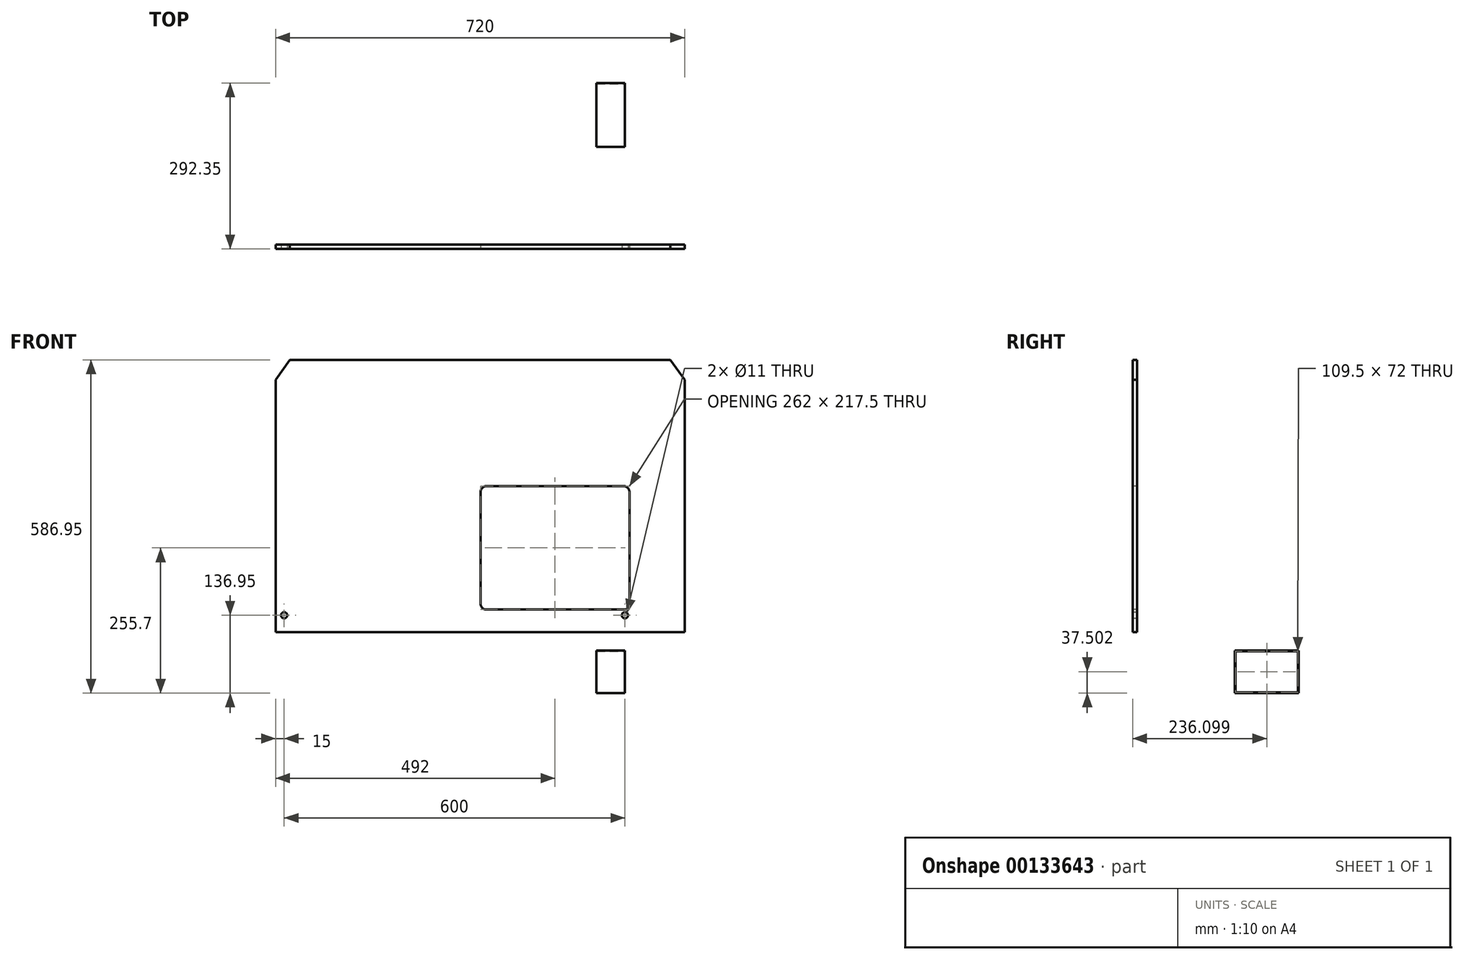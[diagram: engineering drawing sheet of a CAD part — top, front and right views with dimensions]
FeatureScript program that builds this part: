
annotation { "Feature Type Name" : "Feature", "Feature Type Description" : "" }
export const myFeature = defineFeature(function(context is Context, id is Id, definition is map)
    precondition{}
    {
        {
            var Q0;
            Q0=qCreatedBy(makeId("Front.planeOp"),FACE);
            var sketch = newSketch(context, id + "F0", { "sketchPlane" : qUnion([Q0])});
            skLineSegment(sketch, "E0.bottom", {"start": v(-196, 100) * mm, "end": v(-50, 100) * mm});
            skLineSegment(sketch, "E0.top", {"start": v(-196, 207.5) * mm, "end": v(-50, 207.5) * mm});
            skLineSegment(sketch, "E0.left", {"start": v(-196, 100) * mm, "end": v(-196, 207.5) * mm});
            skLineSegment(sketch, "E0.right", {"start": v(-50, 100) * mm, "end": v(-50, 207.5) * mm});
            skLineSegment(sketch, "E1.top", {"start": v(-196, 30) * mm, "end": v(-50, 30) * mm});
            skLineSegment(sketch, "E1.left", {"start": v(-196, 100) * mm, "end": v(-196, 30) * mm});
            skLineSegment(sketch, "E1.right", {"start": v(-50, 100) * mm, "end": v(-50, 30) * mm});
            skLineSegment(sketch, "E2", {"start": v(-196, 207.5) * mm, "end": v(-236, 202.5) * mm});
            skLineSegment(sketch, "E3", {"start": v(-236, 202.5) * mm, "end": v(-236, 105) * mm});
            skLineSegment(sketch, "E4", {"start": v(-236, 105) * mm, "end": v(-196, 100) * mm});
            skLineSegment(sketch, "E5", {"start": v(-123, 207.5) * mm, "end": v(-123, 30) * mm, "construction": true});
            skLineSegment(sketch, "E6", {"start": v(-50, 207.5) * mm, "end": v(-10, 202.5) * mm});
            skLineSegment(sketch, "E7", {"start": v(-10, 202.5) * mm, "end": v(-10, 105) * mm});
            skLineSegment(sketch, "E8", {"start": v(-10, 105) * mm, "end": v(-50, 100) * mm});
            skLineSegment(sketch, "E9", {"start": v(-236, 153.75) * mm, "end": v(-196, 153.75) * mm, "construction": true});
            skLineSegment(sketch, "E10", {"start": v(-50, 153.75) * mm, "end": v(-10, 153.75) * mm, "construction": true});
            skLineSegment(sketch, "E11", {"start": v(-196, 100) * mm, "end": v(-231, 95) * mm});
            skLineSegment(sketch, "E12", {"start": v(-231, 95) * mm, "end": v(-231, 35) * mm});
            skLineSegment(sketch, "E13", {"start": v(-231, 35) * mm, "end": v(-196, 30) * mm});
            skLineSegment(sketch, "E14.MirrorCS", {"start": v(-50, 100) * mm, "end": v(-15, 95) * mm});
            skLineSegment(sketch, "E15.MirrorCS", {"start": v(-15, 95) * mm, "end": v(-15, 35) * mm});
            skLineSegment(sketch, "E16.MirrorCS", {"start": v(-15, 35) * mm, "end": v(-50, 30) * mm});
            skText(sketch, "E17", { "text": "WIDTH", "fontName": "OpenSans-Regular.ttf"});
            const initialGuessF0  = {"E17": [-0.19433, 0.11297, 1, 0, 0.01]};
            skSetInitialGuess(sketch, initialGuessF0);
            skSolve(sketch);
        }
        {
            var Q0;
            Q0=qCreatedBy(makeId("Front.planeOp"),FACE);
            var sketch = newSketch(context, id + "F1", { "sketchPlane" : qUnion([Q0])});
            skLineSegment(sketch, "E18.bottom", {"start": v(-244, 227.5) * mm, "end": v(-2, 227.5) * mm});
            skLineSegment(sketch, "E18.top", {"start": v(-244, 10) * mm, "end": v(-2, 10) * mm});
            skLineSegment(sketch, "E18.left", {"start": v(-254, 217.5) * mm, "end": v(-254, 20) * mm});
            skLineSegment(sketch, "E18.right", {"start": v(8, 217.5) * mm, "end": v(8, 20) * mm});
            skPoint(sketch, "E19.visualSharp", {"position": v(-254, 227.5) * mm});
            skArc(sketch, "E19.filletArc", {"start": v(-244, 227.5) * mm, "mid": v(-251.07, 224.57) * mm, "end": v(-254, 217.5) * mm});
            skPoint(sketch, "E20.visualSharp", {"position": v(8, 227.5) * mm});
            skArc(sketch, "E20.filletArc", {"start": v(8, 217.5) * mm, "mid": v(5.07, 224.57) * mm, "end": v(-2, 227.5) * mm});
            skPoint(sketch, "E21.visualSharp", {"position": v(-254, 10) * mm});
            skArc(sketch, "E21.filletArc", {"start": v(-254, 20) * mm, "mid": v(-251.07, 12.93) * mm, "end": v(-244, 10) * mm});
            skPoint(sketch, "E22.visualSharp", {"position": v(8, 10) * mm});
            skArc(sketch, "E22.filletArc", {"start": v(-2, 10) * mm, "mid": v(5.07, 12.93) * mm, "end": v(8, 20) * mm});
            skLineSegment(sketch, "E23.bottom", {"start": v(-615, 450) * mm, "end": v(105, 450) * mm});
            skLineSegment(sketch, "E23.top", {"start": v(-615, -30) * mm, "end": v(105, -30) * mm});
            skLineSegment(sketch, "E23.left", {"start": v(-615, 450) * mm, "end": v(-615, -30) * mm});
            skLineSegment(sketch, "E23.right", {"start": v(105, 450) * mm, "end": v(105, -30) * mm});
            skCircle(sketch, "E24", {"center": v(0, 0) * mm, "radius": 5.5 * mm});
            skLineSegment(sketch, "E25", {"start": v(0, 0) * mm, "end": v(-600, 0) * mm, "construction": true});
            skCircle(sketch, "E26", {"center": v(-600, 0) * mm, "radius": 5.5 * mm});
            skLineSegment(sketch, "E27", {"start": v(-590, 450) * mm, "end": v(-615, 415) * mm});
            skLineSegment(sketch, "E28", {"start": v(80, 450) * mm, "end": v(105, 415) * mm});
            skLineSegment(sketch, "E29", {"start": v(-255, 450) * mm, "end": v(-255, -30) * mm, "construction": true});
            skSolve(sketch);
        }
        {
            var Q0;
            Q0=makeQuery(id+"F1.imprint","IMPRINT",FACE,{"disambiguationData":[TD([[makeQuery(id+"F1.imprint","IMPRINT",EDGE,{"derivedFrom":sQuery(id+"F1.wireOp",EDGE,"E18.bottom")}),1.0]])]});
            extrude(context, id + "F2", {"entities" : qUnion([Q0]), "oppositeDirection" : true, "depth" : 8 * mm});
        }
        {
            var Q0;
            Q0=qCreatedBy(makeId("Right.planeOp"),FACE);
            var sketch = newSketch(context, id + "F3", { "sketchPlane" : qUnion([Q0])});
            skLineSegment(sketch, "E30.bottom", {"start": v(181.35, -135.45) * mm, "end": v(290.85, -135.45) * mm});
            skLineSegment(sketch, "E30.top", {"start": v(181.35, -63.45) * mm, "end": v(290.85, -63.45) * mm});
            skLineSegment(sketch, "E30.left", {"start": v(181.35, -135.45) * mm, "end": v(181.35, -63.45) * mm});
            skLineSegment(sketch, "E30.right", {"start": v(290.85, -135.45) * mm, "end": v(290.85, -63.45) * mm});
            skLineSegment(sketch, "E31.0", {"start": v(179.85, -61.95) * mm, "end": v(292.35, -61.95) * mm});
            skLineSegment(sketch, "E31.1", {"start": v(179.85, -136.95) * mm, "end": v(179.85, -61.95) * mm});
            skLineSegment(sketch, "E31.2", {"start": v(179.85, -136.95) * mm, "end": v(292.35, -136.95) * mm});
            skLineSegment(sketch, "E31.3", {"start": v(292.35, -136.95) * mm, "end": v(292.35, -61.95) * mm});
            skSolve(sketch);
        }
        {
            var Q0;
            Q0=makeQuery(id+"F3.imprint","IMPRINT",FACE,{"disambiguationData":[TD([[makeQuery(id+"F3.imprint","IMPRINT",EDGE,{"derivedFrom":sQuery(id+"F3.wireOp",EDGE,"E30.bottom")}),-1.0]])]});
            extrude(context, id + "F4", {"entities" : qUnion([Q0]), "oppositeDirection" : true, "depth" : 50 * mm});
        }
    });
